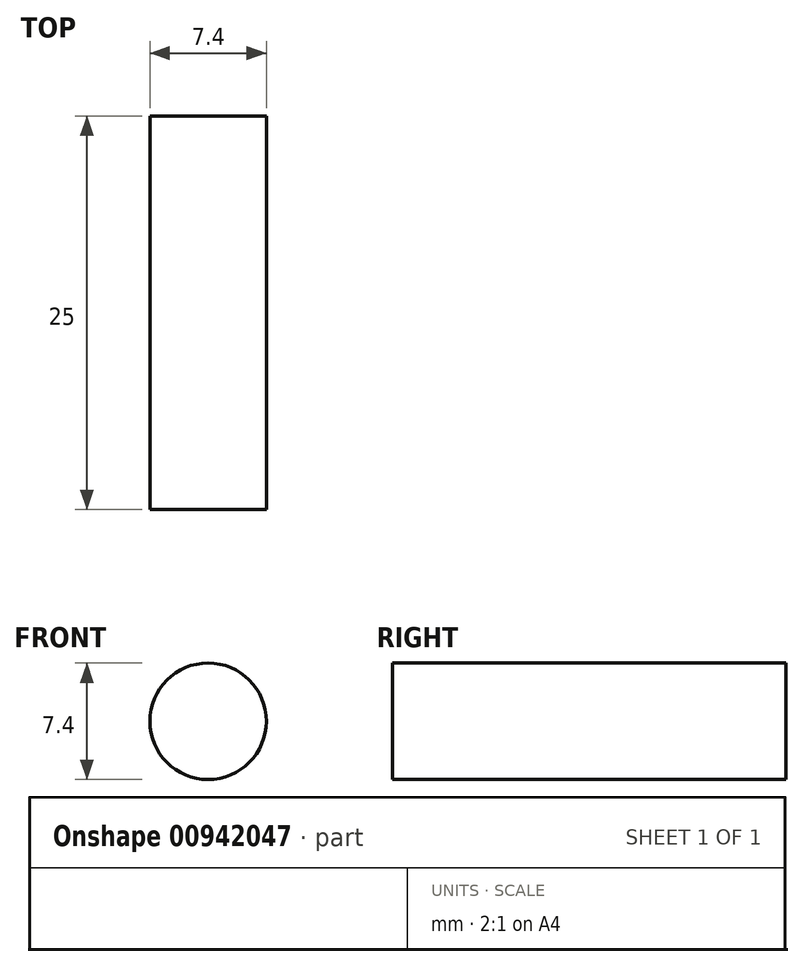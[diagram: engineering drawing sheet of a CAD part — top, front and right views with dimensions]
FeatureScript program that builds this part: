
annotation { "Feature Type Name" : "Feature", "Feature Type Description" : "" }
export const myFeature = defineFeature(function(context is Context, id is Id, definition is map)
    precondition{}
    {
        {
            var Q0;
            Q0=qCreatedBy(makeId("Front.planeOp"),FACE);
            var sketch = newSketch(context, id + "F0", { "sketchPlane" : qUnion([Q0])});
            skCircle(sketch, "E0", {"center": v(0, 0) * mm, "radius": 3.7 * mm});
            skSolve(sketch);
        }
        {
            var Q0;
            Q0=makeQuery(id+"F0.imprint","IMPRINT",FACE,{"disambiguationData":[TD([[makeQuery(id+"F0.imprint","IMPRINT",EDGE,{"derivedFrom":sQuery(id+"F0.wireOp",EDGE,"E0")}),1.0]])]});
            extrude(context, id + "F1", {"entities" : qUnion([Q0]), "depth" : 25 * mm, "offsetDistance" : 25 * mm});
        }
    });
